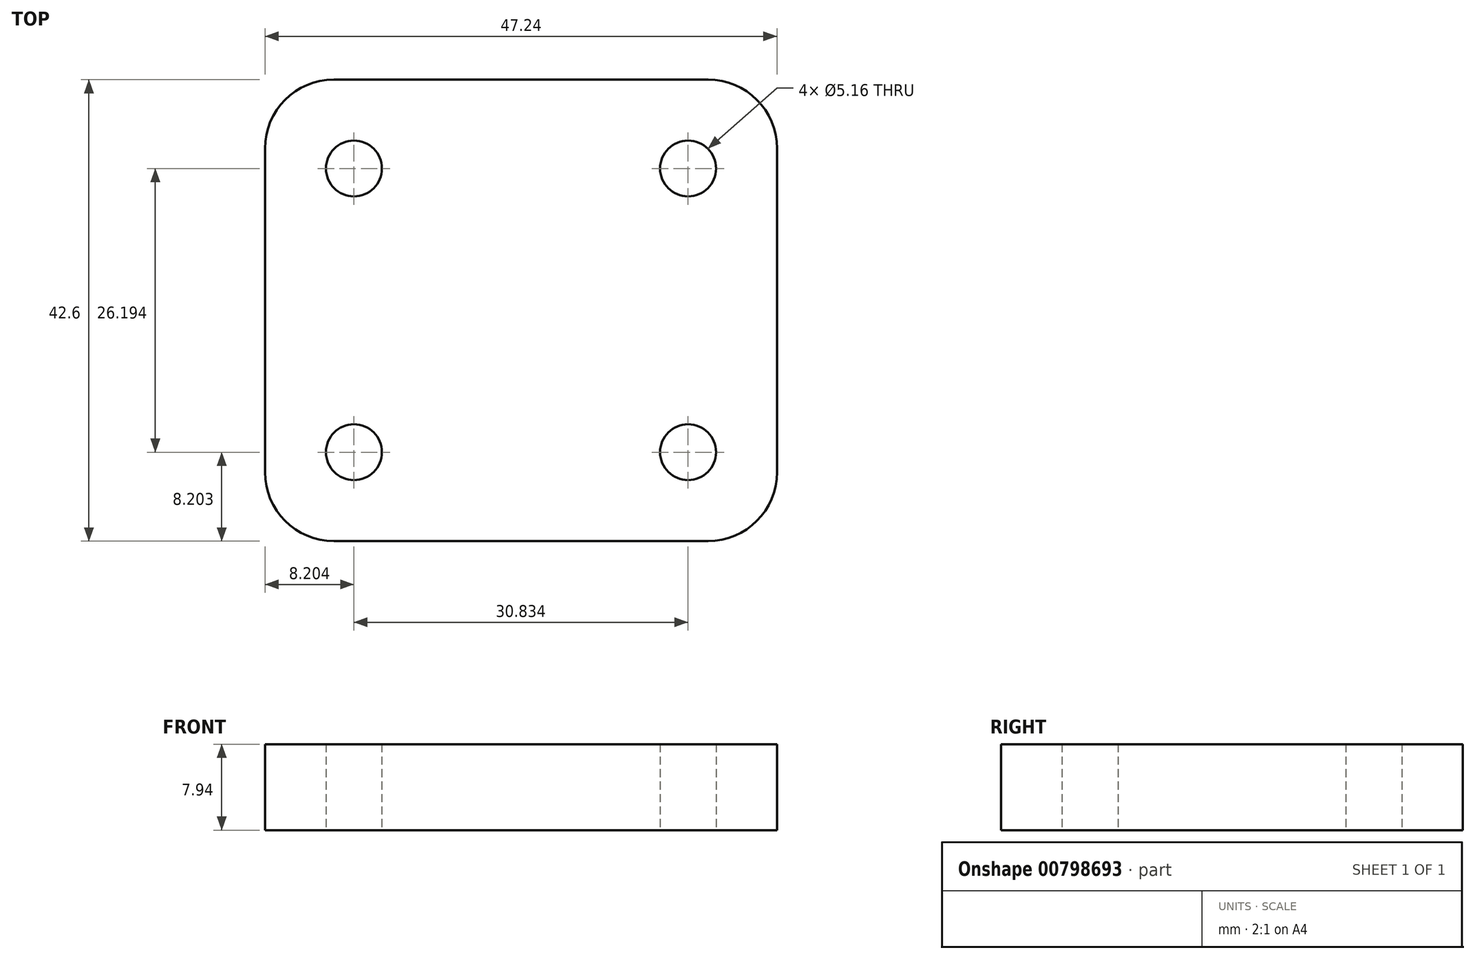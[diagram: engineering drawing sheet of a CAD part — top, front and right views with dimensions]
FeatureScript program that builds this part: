
annotation { "Feature Type Name" : "Feature", "Feature Type Description" : "" }
export const myFeature = defineFeature(function(context is Context, id is Id, definition is map)
    precondition{}
    {
        {
            var Q0;
            Q0=qCreatedBy(makeId("Top.planeOp"),FACE);
            var sketch = newSketch(context, id + "F0", { "sketchPlane" : qUnion([Q0])});
            skLineSegment(sketch, "E0.bottom", {"start": v(-150.3, -57.52) * mm, "end": v(-115.76, -57.52) * mm});
            skLineSegment(sketch, "E0.top", {"start": v(-150.3, -14.92) * mm, "end": v(-115.76, -14.92) * mm});
            skLineSegment(sketch, "E0.left", {"start": v(-156.65, -51.17) * mm, "end": v(-156.65, -21.27) * mm});
            skLineSegment(sketch, "E0.right", {"start": v(-109.4, -51.17) * mm, "end": v(-109.4, -21.27) * mm});
            skCircle(sketch, "E1", {"center": v(-148.45, -49.32) * mm, "radius": 2.58 * mm});
            skCircle(sketch, "E2.0.1.0", {"center": v(-148.45, -23.12) * mm, "radius": 2.58 * mm});
            skCircle(sketch, "E2.1.0.0", {"center": v(-117.61, -49.32) * mm, "radius": 2.58 * mm});
            skCircle(sketch, "E2.1.1.0", {"center": v(-117.61, -23.12) * mm, "radius": 2.58 * mm});
            skLineSegment(sketch, "E2.direction1", {"start": v(-148.45, -49.32) * mm, "end": v(-117.61, -49.32) * mm, "construction": true});
            skLineSegment(sketch, "E2.direction2", {"start": v(-148.45, -49.32) * mm, "end": v(-148.45, -23.12) * mm, "construction": true});
            skPoint(sketch, "E3.visualSharp", {"position": v(-109.4, -14.92) * mm});
            skArc(sketch, "E3.filletArc", {"start": v(-109.4, -21.27) * mm, "mid": v(-111.27, -16.78) * mm, "end": v(-115.76, -14.92) * mm});
            skPoint(sketch, "E4.visualSharp", {"position": v(-156.65, -14.92) * mm});
            skArc(sketch, "E4.filletArc", {"start": v(-150.3, -14.92) * mm, "mid": v(-154.8, -16.78) * mm, "end": v(-156.65, -21.27) * mm});
            skPoint(sketch, "E5.visualSharp", {"position": v(-109.4, -57.52) * mm});
            skArc(sketch, "E5.filletArc", {"start": v(-115.76, -57.52) * mm, "mid": v(-111.27, -55.66) * mm, "end": v(-109.4, -51.17) * mm});
            skPoint(sketch, "E6.visualSharp", {"position": v(-156.65, -57.52) * mm});
            skArc(sketch, "E6.filletArc", {"start": v(-156.65, -51.17) * mm, "mid": v(-154.8, -55.66) * mm, "end": v(-150.3, -57.52) * mm});
            skSolve(sketch);
        }
        {
            var Q0;
            Q0=makeQuery(id+"F0.imprint","IMPRINT",FACE,{"disambiguationData":[TD([[makeQuery(id+"F0.imprint","IMPRINT",EDGE,{"derivedFrom":sQuery(id+"F0.wireOp",EDGE,"E0.bottom")}),1.0]])]});
            extrude(context, id + "F1", {"entities" : qUnion([Q0]), "depth" : 7.94 * mm, "offsetDistance" : 25.4 * mm});
        }
    });
